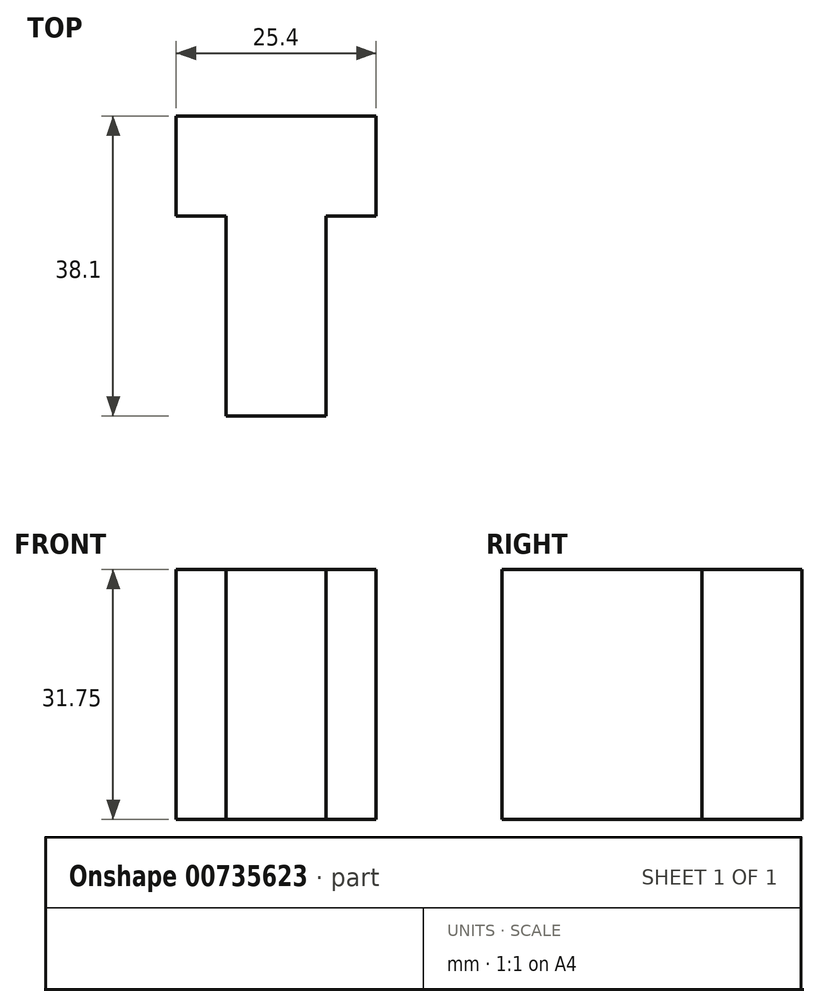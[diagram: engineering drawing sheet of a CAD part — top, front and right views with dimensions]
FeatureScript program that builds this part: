
annotation { "Feature Type Name" : "Feature", "Feature Type Description" : "" }
export const myFeature = defineFeature(function(context is Context, id is Id, definition is map)
    precondition{}
    {
        {
            var Q0;
            Q0=qCreatedBy(makeId("Top.planeOp"),FACE);
            var sketch = newSketch(context, id + "F0", { "sketchPlane" : qUnion([Q0])});
            skLineSegment(sketch, "E0", {"start": v(0, 0) * mm, "end": v(25.4, 0) * mm});
            skLineSegment(sketch, "E1", {"start": v(25.4, 0) * mm, "end": v(25.4, -12.7) * mm});
            skLineSegment(sketch, "E2", {"start": v(25.4, -12.7) * mm, "end": v(19.05, -12.7) * mm});
            skLineSegment(sketch, "E3", {"start": v(19.05, -12.7) * mm, "end": v(19.05, -38.1) * mm});
            skLineSegment(sketch, "E4", {"start": v(19.05, -38.1) * mm, "end": v(6.35, -38.1) * mm});
            skLineSegment(sketch, "E5", {"start": v(6.35, -38.1) * mm, "end": v(6.35, -12.7) * mm});
            skLineSegment(sketch, "E6", {"start": v(6.35, -12.7) * mm, "end": v(0, -12.7) * mm});
            skLineSegment(sketch, "E7", {"start": v(0, -12.7) * mm, "end": v(0, 0) * mm});
            skSolve(sketch);
        }
        {
            var Q0;
            Q0=makeQuery(id+"F0.imprint","IMPRINT",FACE,{"disambiguationData":[TD([[makeQuery(id+"F0.imprint","IMPRINT",EDGE,{"derivedFrom":sQuery(id+"F0.wireOp",EDGE,"E0")}),-1.0]])]});
            extrude(context, id + "F1", {"entities" : qUnion([Q0]), "depth" : 31.75 * mm, "offsetDistance" : 25.4 * mm});
        }
    });
